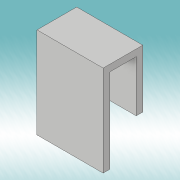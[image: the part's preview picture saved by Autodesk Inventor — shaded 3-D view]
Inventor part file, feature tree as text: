
AUTODESK INVENTOR PART (.ipt)
format: ipt  version: 2019 (Build 230136000, 136)  size: 115,200 bytes
history: native  units: mm
features: extrude x4, sketch x3
ambient origin geometry x8: Origin, YZ Plane, XZ Plane, XY Plane, X Axis, Y Axis, Z Axis, Center Point
bodies: Solid1 (feature_tree)
feature tree (7):
  sketch  "Sketch1"  dims[d15=40.0mm d16=20.0mm]
  extrude  "Extrusion1"  Depth=20.0mm
  extrude  "Extrusion2"  Depth=18.0mm
  extrude  "Extrusion3"  Depth=4.0mm TaperAngle=0.0deg
  extrude  "Extrusion4"  Depth=4.0mm
  sketch  "Sketch2"  dims[d17=38.0mm d18=18.0mm]
  sketch  "Sketch3"  dims[d19=35.0mm d20=4.0mm d21=0.0mm d22=4.0mm d23=40.0mm d24=16.0mm d25=0.0mm d26=55.0mm d27=40.0mm d28=4.0mm d29=0.0mm d30=0.1mm d31=0.0mm]
